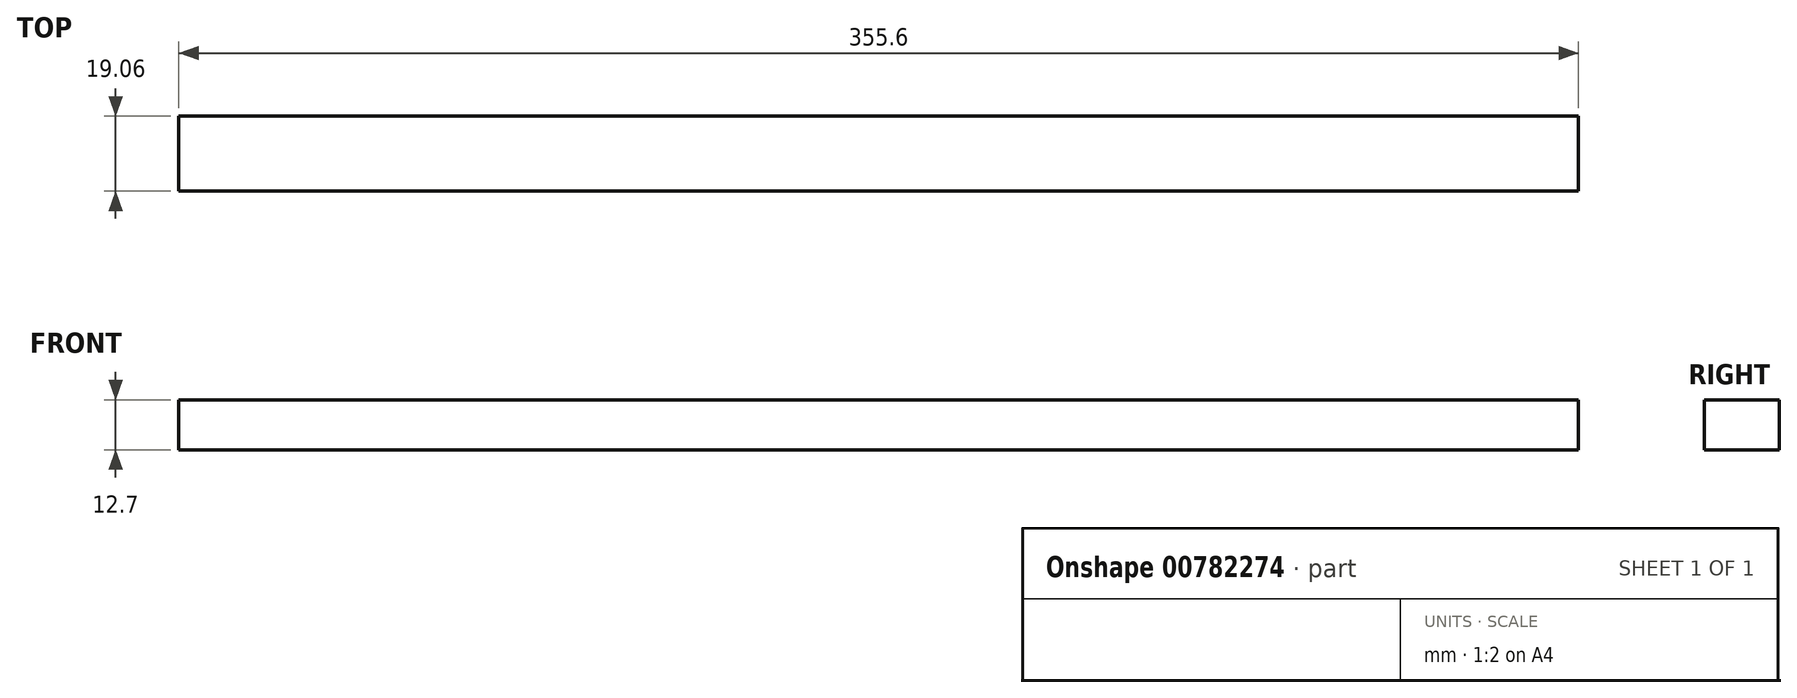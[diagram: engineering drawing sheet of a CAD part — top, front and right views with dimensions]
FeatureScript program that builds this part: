
annotation { "Feature Type Name" : "Feature", "Feature Type Description" : "" }
export const myFeature = defineFeature(function(context is Context, id is Id, definition is map)
    precondition{}
    {
        {
            var Q0;
            Q0=qCreatedBy(makeId("Front.planeOp"),FACE);
            var sketch = newSketch(context, id + "F0", { "sketchPlane" : qUnion([Q0])});
            skLineSegment(sketch, "E0.bottom", {"start": v(-177.8, 6.35) * mm, "end": v(177.8, 6.35) * mm});
            skLineSegment(sketch, "E0.top", {"start": v(-177.8, -6.35) * mm, "end": v(177.8, -6.35) * mm});
            skLineSegment(sketch, "E0.left", {"start": v(-177.8, 6.35) * mm, "end": v(-177.8, -6.35) * mm});
            skLineSegment(sketch, "E0.right", {"start": v(177.8, 6.35) * mm, "end": v(177.8, -6.35) * mm});
            skLineSegment(sketch, "E1", {"start": v(-177.8, 6.35) * mm, "end": v(177.8, -6.35) * mm, "construction": true});
            skSolve(sketch);
        }
        {
            var Q0;
            Q0 = qSketchRegion(id + "F0", true);
            extrude(context, id + "F1", {"entities" : qUnion([Q0]), "endBound" : BoundingType.SYMMETRIC, "depth" : 19.05 * mm, "offsetDistance" : 25.4 * mm});
        }
    });
